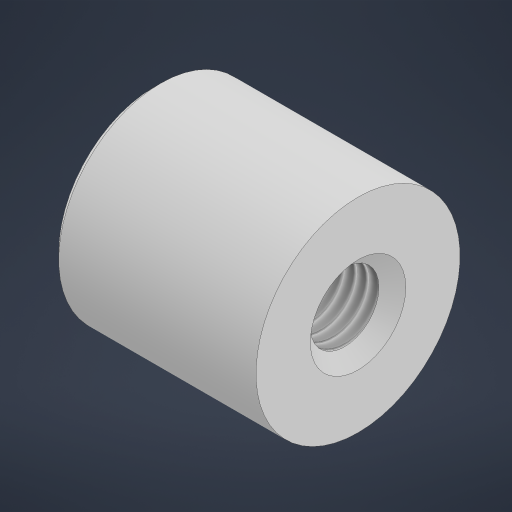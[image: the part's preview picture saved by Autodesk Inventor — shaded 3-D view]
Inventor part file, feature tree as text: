
AUTODESK INVENTOR PART (.ipt)
format: ipt  version: 2024.1 (Build 281209000, 209)  size: 188,928 bytes
history: native  units: mm
features: sketch x2, revolve x1, hole x1, chamfer x1
ambient origin geometry x8: Origin, YZ Plane, XZ Plane, XY Plane, X Axis, Y Axis, Z Axis, Center Point
bodies: Solid1 (feature_tree)
feature tree (5):
  revolve  "Revolution1"  [1 undecoded]
  hole  "Hole1"  [1 undecoded]
  chamfer  "Chamfer1"  [1 undecoded]
  sketch  "Sketch1"  dims[d0=30.0mm d1=30.0mm]
  sketch  "Sketch2"  dims[d2=90.0deg d3=10.106mm d4=10.0mm d5=14.05mm d6=2.0mm d7=90.0deg d8=15.0mm d9=20.594885mm d10=1.0mm d11=2.0mm d12=45.0deg]
note: 3 required parameter values undecoded (feature->parameter linkage not recoverable at this tier; creation-order binding heuristic only, values carry confidence <= 0.55)